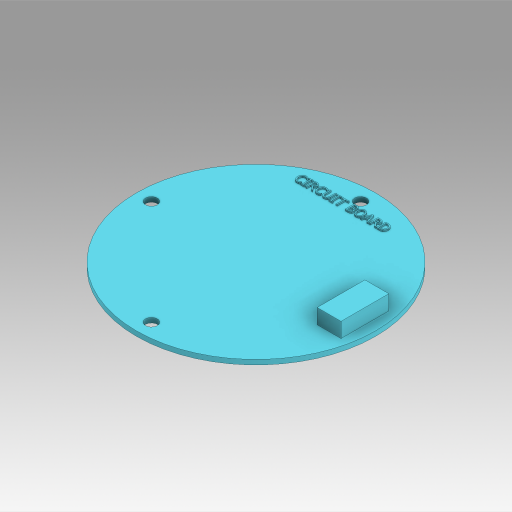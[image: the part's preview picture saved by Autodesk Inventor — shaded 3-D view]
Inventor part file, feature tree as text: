
AUTODESK INVENTOR PART (.ipt)
format: ipt  version: 2023 (Build 270158000, 158)  size: 557,056 bytes
history: native  units: in
note: dims shown in document units (in); Inventor stores cm internally (conversion verified against a paired STEP export)
features: sketch x4, extrude x3, emboss x1, projected_geometry x1
ambient origin geometry x8: Origin, YZ Plane, XZ Plane, XY Plane, X Axis, Y Axis, Z Axis, Center Point
bodies: Solid1 (feature_tree)
feature tree (9):
  extrude  "Extrusion1"  Depth=0.063in TaperAngle=0.0deg
  extrude  "Extrusion2"  Depth=1.435in
  emboss  "Emboss1"
  extrude  "Extrusion3"  Depth=0.1969in TaperAngle=0.0deg
  sketch  "Sketch1"  dims[d0=3.1496in d1=0.063in d2=0.0in]
  sketch  "Sketch2"  dims[d3=0.6299in d4=1.435in]
  sketch  "Sketch3"  dims[d5=0.315in d6=0.1969in d7=0.0in]
  sketch  "Sketch4"  dims[d8=0.0197in d9=0.0in d16=0.1575in d17=0.1969in d18=0.1575in d19=0.1969in d20=0.1575in d21=0.1969in d22=0.0in d23=0.0in]
  projected_geometry  "Projected Loop1"
